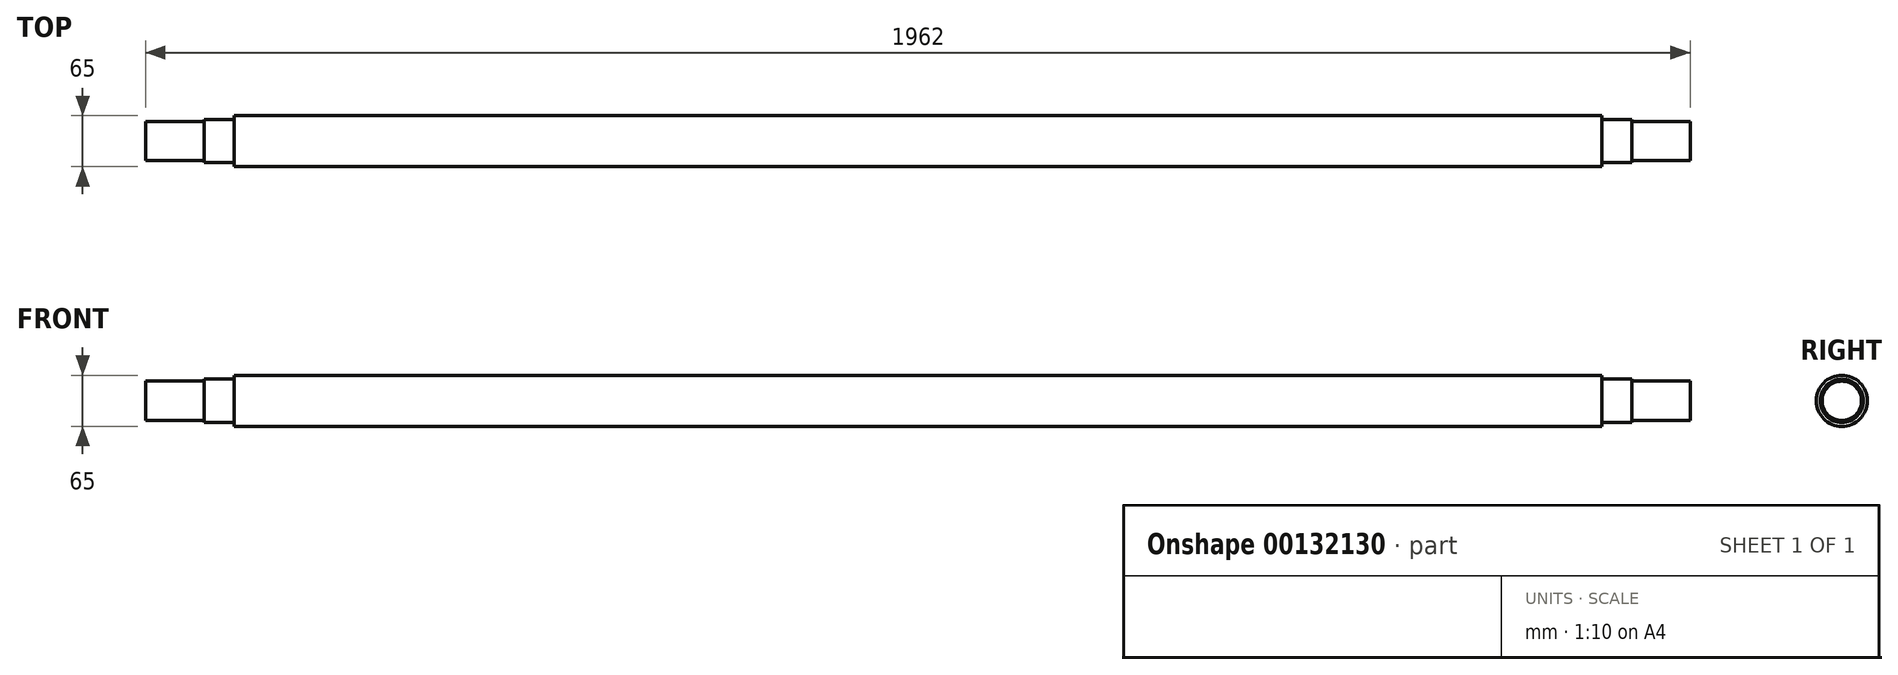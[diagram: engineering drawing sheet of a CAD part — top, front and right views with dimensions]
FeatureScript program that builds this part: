
annotation { "Feature Type Name" : "Feature", "Feature Type Description" : "" }
export const myFeature = defineFeature(function(context is Context, id is Id, definition is map)
    precondition{}
    {
        {
            var Q0;
            Q0=qCreatedBy(makeId("Right.planeOp"),FACE);
            var sketch = newSketch(context, id + "F0", { "sketchPlane" : qUnion([Q0])});
            skCircle(sketch, "E0", {"center": v(0, 0) * mm, "radius": 32.5 * mm});
            skSolve(sketch);
        }
        {
            var Q0;
            Q0 = qSketchRegion(id + "F0", true);
            extrude(context, id + "F1", {"entities" : qUnion([Q0]), "endBound" : BoundingType.SYMMETRIC, "depth" : 1737 * mm});
        }
        {
            var Q0;
            Q0=makeQuery(id+"F1.opExtrude","CAP_FACE",FACE,{"disambiguationData":[OSD([sQuery(id+"F0.wireOp",EDGE,"E0")])],"isStart":false});
            var sketch = newSketch(context, id + "F2", { "sketchPlane" : qUnion([Q0])});
            skCircle(sketch, "E1", {"center": v(0, 0) * mm, "radius": 27.5 * mm});
            skSolve(sketch);
        }
        {
            var Q0;
            Q0 = qSketchRegion(id + "F2", true);
            extrude(context, id + "F3", {"entities" : qUnion([Q0]), "depth" : 38.5 * mm});
        }
        {
            var Q0;
            Q0=makeQuery(id+"F3.opExtrude","CAP_FACE",FACE,{"disambiguationData":[OSD([sQuery(id+"F2.wireOp",EDGE,"E1")])],"isStart":false});
            var sketch = newSketch(context, id + "F4", { "sketchPlane" : qUnion([Q0])});
            skCircle(sketch, "E2", {"center": v(0, 0) * mm, "radius": 25 * mm});
            skSolve(sketch);
        }
        {
            var Q0;
            Q0 = qSketchRegion(id + "F4", true);
            extrude(context, id + "F5", {"entities" : qUnion([Q0]), "operationType" : NewBodyOperationType.ADD, "depth" : 74 * mm});
        }
        {
            var Q0;
            Q0=makeQuery(id+"F3.opExtrude","SWEPT_BODY",BODY,{"disambiguationData":[OSD([sQuery(id+"F2.wireOp",EDGE,"E1")])]});
            var Q1;
            Q1=qCreatedBy(makeId("Right.planeOp"),FACE);
            mirror(context, id + "F6", {"operationType" : NewBodyOperationType.ADD, "entities" : qUnion([Q0]), "mirrorPlane" : qUnion([Q1])});
        }
    });
